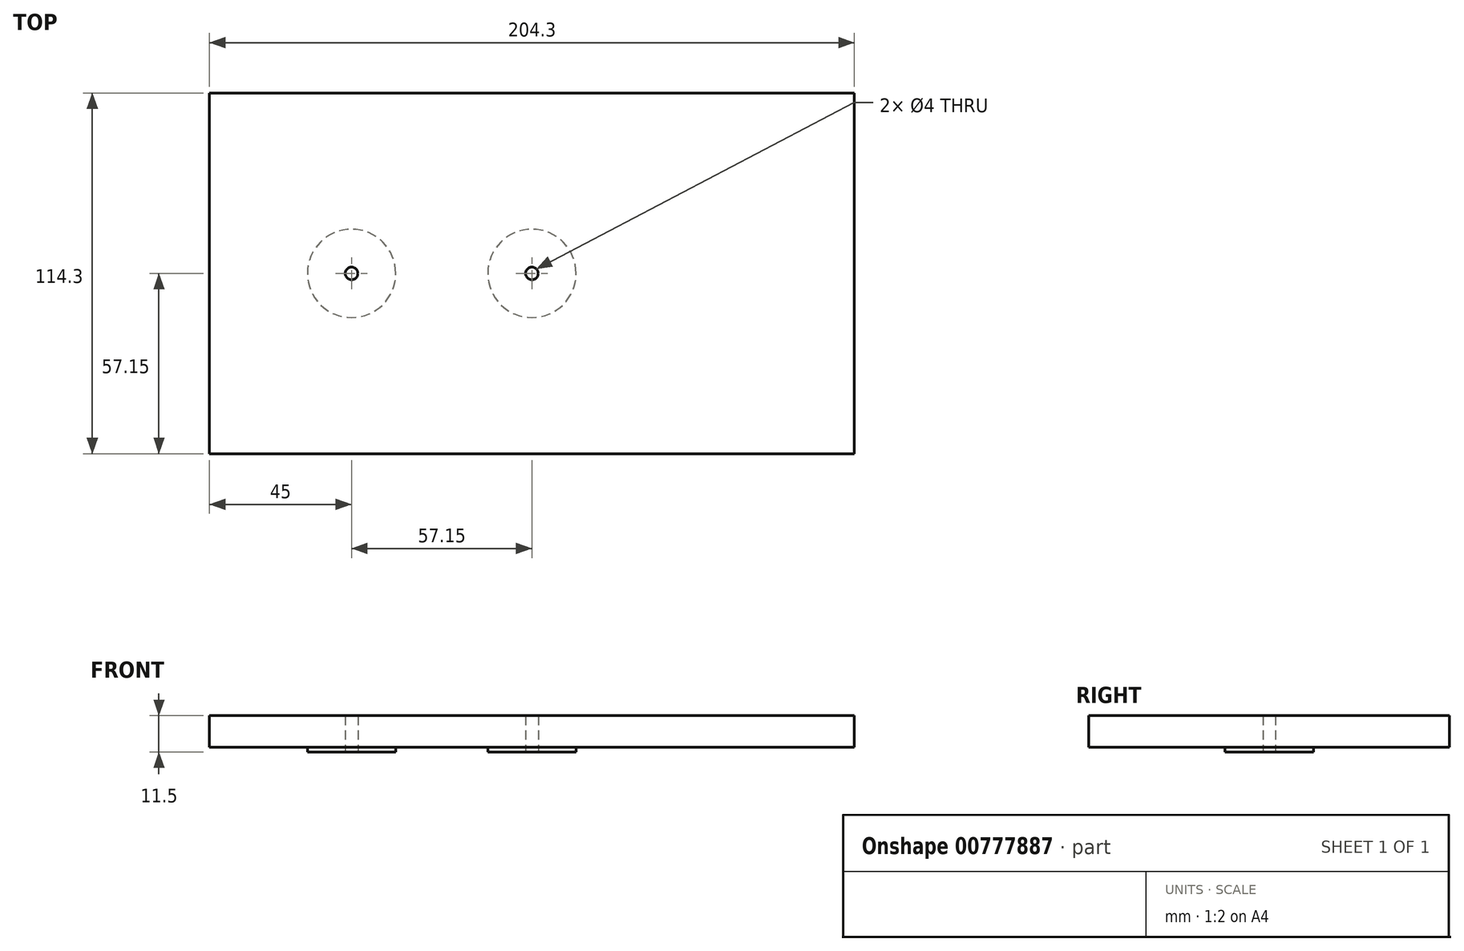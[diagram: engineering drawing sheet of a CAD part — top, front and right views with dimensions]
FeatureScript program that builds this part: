
annotation { "Feature Type Name" : "Feature", "Feature Type Description" : "" }
export const myFeature = defineFeature(function(context is Context, id is Id, definition is map)
    precondition{}
    {
        {
            var Q0;
            Q0=qCreatedBy(makeId("Top.planeOp"),FACE);
            var sketch = newSketch(context, id + "F0", { "sketchPlane" : qUnion([Q0])});
            skLineSegment(sketch, "E0.bottom", {"start": v(102.15, 57.15) * mm, "end": v(-102.15, 57.15) * mm});
            skLineSegment(sketch, "E0.top", {"start": v(102.15, -57.15) * mm, "end": v(-102.15, -57.15) * mm});
            skLineSegment(sketch, "E0.left", {"start": v(102.15, 57.15) * mm, "end": v(102.15, -57.15) * mm});
            skLineSegment(sketch, "E0.right", {"start": v(-102.15, 57.15) * mm, "end": v(-102.15, -57.15) * mm});
            skPoint(sketch, "E0.middle", {"position": v(0, 0) * mm});
            skPoint(sketch, "E1", {"position": v(-57.15, 0) * mm});
            skCircle(sketch, "E2", {"center": v(-57.15, 0) * mm, "radius": 14 * mm});
            skCircle(sketch, "E3", {"center": v(0, 0) * mm, "radius": 14 * mm});
            skSolve(sketch);
        }
        {
            var Q0;
            Q0 = qSketchRegion(id + "F0", true);
            var Q1;
            Q1=makeQuery(id+"F0.imprint","IMPRINT",FACE,{"disambiguationData":[TD([[makeQuery(id+"F0.imprint","IMPRINT",EDGE,{"derivedFrom":sQuery(id+"F0.wireOp",EDGE,"E2")}),1.0]])]});
            var Q2;
            Q2=makeQuery(id+"F0.imprint","IMPRINT",FACE,{"disambiguationData":[TD([[makeQuery(id+"F0.imprint","IMPRINT",EDGE,{"derivedFrom":sQuery(id+"F0.wireOp",EDGE,"E3")}),1.0]])]});
            extrude(context, id + "F1", {"entities" : qUnion([Q0, Q1, Q2]), "depth" : 10 * mm, "offsetDistance" : 25 * mm});
        }
        {
            var Q0;
            Q0=makeQuery(id+"F0.imprint","IMPRINT",FACE,{"disambiguationData":[TD([[makeQuery(id+"F0.imprint","IMPRINT",EDGE,{"derivedFrom":sQuery(id+"F0.wireOp",EDGE,"E2")}),1.0]])]});
            var Q1;
            Q1=makeQuery(id+"F0.imprint","IMPRINT",FACE,{"disambiguationData":[TD([[makeQuery(id+"F0.imprint","IMPRINT",EDGE,{"derivedFrom":sQuery(id+"F0.wireOp",EDGE,"E3")}),1.0]])]});
            extrude(context, id + "F2", {"entities" : qUnion([Q0, Q1]), "operationType" : NewBodyOperationType.ADD, "oppositeDirection" : true, "depth" : 1.5 * mm, "offsetDistance" : 25 * mm});
        }
        {
            var Q0;
            Q0=makeQuery(id+"F2.opExtrude","CAP_FACE",FACE,{"disambiguationData":[OSD([sQuery(id+"F0.wireOp",EDGE,"E3")])],"isStart":false});
            var sketch = newSketch(context, id + "F3", { "sketchPlane" : qUnion([Q0])});
            skPoint(sketch, "E4.0", {"position": v(-57.15, 0) * mm});
            skPoint(sketch, "E4.1", {"position": v(0, 0) * mm});
            skSolve(sketch);
        }
        {
            var Q0;
            Q0=sQuery(id+"F3.wireOp",VERTEX,"E4.0");
            var Q1;
            Q1=sQuery(id+"F3.wireOp",VERTEX,"E4.1");
            var Q2;
            Q2=makeQuery(id+"F1.opExtrude","SWEPT_BODY",BODY,{"disambiguationData":[OSD([sQuery(id+"F0.wireOp",EDGE,"E0.bottom"),sQuery(id+"F0.wireOp",EDGE,"E0.top"),sQuery(id+"F0.wireOp",EDGE,"E0.left"),sQuery(id+"F0.wireOp",EDGE,"E0.right")])]});
            hole(context, id + "F4", {"style" : HoleStyle.SIMPLE, "endStyle" : HoleEndStyle.THROUGH, "holeDiameter" : 4 * mm, "majorDiameter" : 5 * mm, "isTappedThrough" : true, "tappedDepth" : 12 * mm, "tapClearance" : 3, "startFromSketch" : true, "locations" : qUnion([Q0, Q1]), "scope" : qUnion([Q2])});
        }
    });
